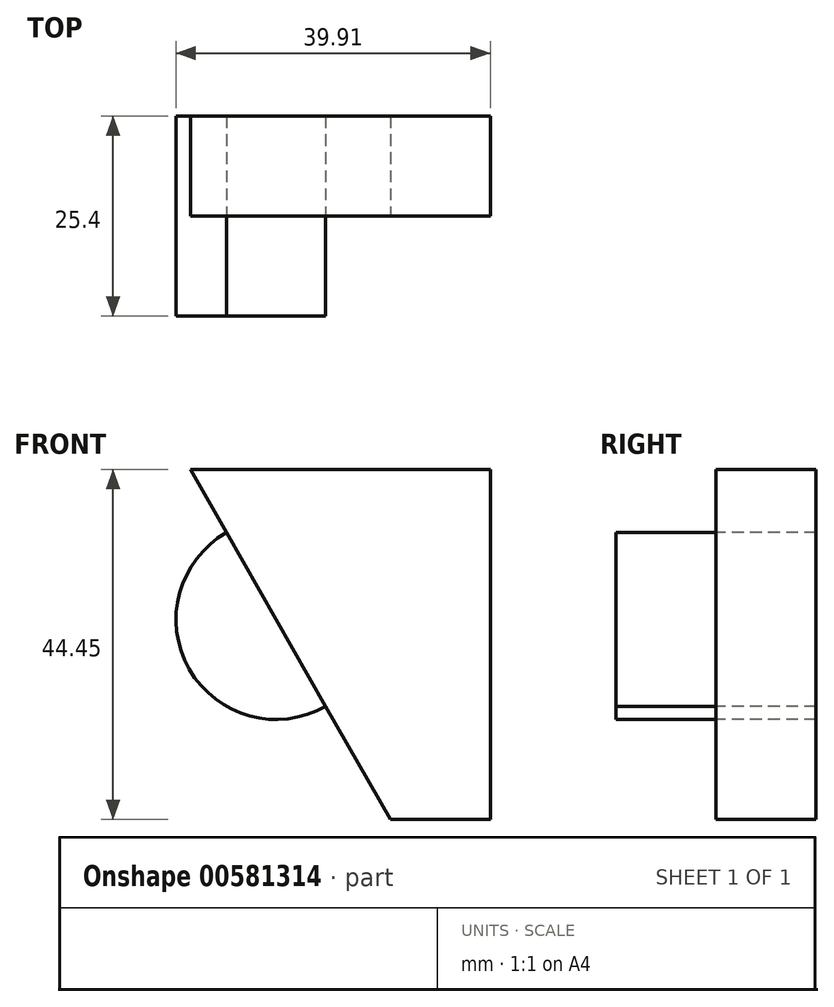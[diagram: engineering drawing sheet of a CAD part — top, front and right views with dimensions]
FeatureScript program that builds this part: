
annotation { "Feature Type Name" : "Feature", "Feature Type Description" : "" }
export const myFeature = defineFeature(function(context is Context, id is Id, definition is map)
    precondition{}
    {
        {
            var Q0;
            Q0=qCreatedBy(makeId("Front.planeOp"),FACE);
            var sketch = newSketch(context, id + "F0", { "sketchPlane" : qUnion([Q0])});
            skLineSegment(sketch, "E0.bottom", {"start": v(-20.36, 31.68) * mm, "end": v(36.8, 31.68) * mm});
            skLineSegment(sketch, "E0.top", {"start": v(-20.36, -12.77) * mm, "end": v(36.8, -12.77) * mm});
            skLineSegment(sketch, "E0.left", {"start": v(-20.36, 31.68) * mm, "end": v(-20.36, -12.77) * mm});
            skLineSegment(sketch, "E0.right", {"start": v(36.8, 31.68) * mm, "end": v(36.8, -12.77) * mm});
            skSolve(sketch);
        }
        {
            var Q0;
            Q0 = qSketchRegion(id + "F0", true);
            extrude(context, id + "F1", {"entities" : qUnion([Q0]), "depth" : 25.4 * mm, "offsetDistance" : 25.4 * mm});
        }
        {
            var Q0;
            Q0=makeQuery(id+"F1.opExtrude","CAP_FACE",FACE,{"disambiguationData":[OSD([sQuery(id+"F0.wireOp",EDGE,"E0.bottom"),sQuery(id+"F0.wireOp",EDGE,"E0.top"),sQuery(id+"F0.wireOp",EDGE,"E0.left"),sQuery(id+"F0.wireOp",EDGE,"E0.right")])],"isStart":false});
            var sketch = newSketch(context, id + "F2", { "sketchPlane" : qUnion([Q0])});
            skLineSegment(sketch, "E1", {"start": v(-1.3, 31.68) * mm, "end": v(24.1, -12.77) * mm});
            skLineSegment(sketch, "E2", {"start": v(24.1, -12.77) * mm, "end": v(36.8, -12.77) * mm});
            skLineSegment(sketch, "E3", {"start": v(36.8, -12.77) * mm, "end": v(36.8, 31.68) * mm});
            skLineSegment(sketch, "E4", {"start": v(36.8, 31.68) * mm, "end": v(-1.3, 31.68) * mm});
            skSolve(sketch);
        }
        {
            var Q0;
            Q0 = qSketchRegion(id + "F2", true);
            extrude(context, id + "F3", {"entities" : qUnion([Q0]), "operationType" : NewBodyOperationType.REMOVE, "oppositeDirection" : true, "depth" : 12.7 * mm, "offsetDistance" : 25.4 * mm});
        }
        {
            var Q0;
            Q0=makeQuery(id+"F1.opExtrude","CAP_FACE",FACE,{"disambiguationData":[OSD([sQuery(id+"F0.wireOp",EDGE,"E0.bottom"),sQuery(id+"F0.wireOp",EDGE,"E0.top"),sQuery(id+"F0.wireOp",EDGE,"E0.left"),sQuery(id+"F0.wireOp",EDGE,"E0.right")])],"isStart":false});
            var sketch = newSketch(context, id + "F4", { "sketchPlane" : qUnion([Q0])});
            skLineSegment(sketch, "E5", {"start": v(-20.36, -12.77) * mm, "end": v(-20.36, 12.63) * mm});
            skLineSegment(sketch, "E6", {"start": v(-20.36, 12.63) * mm, "end": v(36.75, 12.63) * mm});
            skCircle(sketch, "E7", {"center": v(9.58, 12.63) * mm, "radius": 12.7 * mm});
            skSolve(sketch);
        }
        {
            var Q0;
            {var subQ0=sQuery(id+"F4.wireOp",EDGE,"E7");var subQ1=sQuery(id+"F4.wireOp",EDGE,"E6");var subQ2=makeQuery(id+"F4.imprint","INTERSECT",VERTEX,{"disambiguationData":[OD(1.0)],"derivedFrom":[subQ1,subQ0]});Q0=makeQuery(id+"F4.imprint","IMPRINT",FACE,{"disambiguationData":[TD([[makeQuery(id+"F4.imprint","IMPRINT",EDGE,{"disambiguationData":[TD([[subQ2,-1.0]])],"derivedFrom":subQ1}),1.0]])]});}
            var Q1;
            {var subQ0=sQuery(id+"F4.wireOp",EDGE,"E7");var subQ1=sQuery(id+"F4.wireOp",EDGE,"E6");var subQ2=makeQuery(id+"F4.imprint","INTERSECT",VERTEX,{"disambiguationData":[OD(0.0)],"derivedFrom":[subQ1,subQ0]});Q1=makeQuery(id+"F4.imprint","IMPRINT",FACE,{"disambiguationData":[TD([[makeQuery(id+"F4.imprint","IMPRINT",EDGE,{"disambiguationData":[TD([[subQ2,1.0]])],"derivedFrom":subQ1}),-1.0]])]});}
            var Q2;
            {var subQ0=sQuery(id+"F4.wireOp",EDGE,"E7");var subQ1=sQuery(id+"F4.wireOp",EDGE,"E6");var subQ2=makeQuery(id+"F4.imprint","INTERSECT",VERTEX,{"disambiguationData":[OD(1.0)],"derivedFrom":[subQ1,subQ0]});Q2=makeQuery(id+"F4.imprint","IMPRINT",FACE,{"disambiguationData":[TD([[makeQuery(id+"F4.imprint","IMPRINT",EDGE,{"disambiguationData":[TD([[subQ2,-1.0]])],"derivedFrom":subQ1}),-1.0]])]});}
            var Q3;
            {var subQ0=sQuery(id+"F4.wireOp",EDGE,"E7");var subQ1=sQuery(id+"F4.wireOp",EDGE,"E6");var subQ2=makeQuery(id+"F4.imprint","INTERSECT",VERTEX,{"disambiguationData":[OD(0.0)],"derivedFrom":[subQ1,subQ0]});Q3=makeQuery(id+"F4.imprint","IMPRINT",FACE,{"disambiguationData":[TD([[makeQuery(id+"F4.imprint","IMPRINT",EDGE,{"disambiguationData":[TD([[subQ2,1.0]])],"derivedFrom":subQ1}),1.0]])]});}
            extrude(context, id + "F5", {"entities" : qUnion([Q0, Q1, Q2, Q3]), "operationType" : NewBodyOperationType.REMOVE, "oppositeDirection" : true, "depth" : 25.4 * mm, "offsetDistance" : 25.4 * mm});
        }
    });
